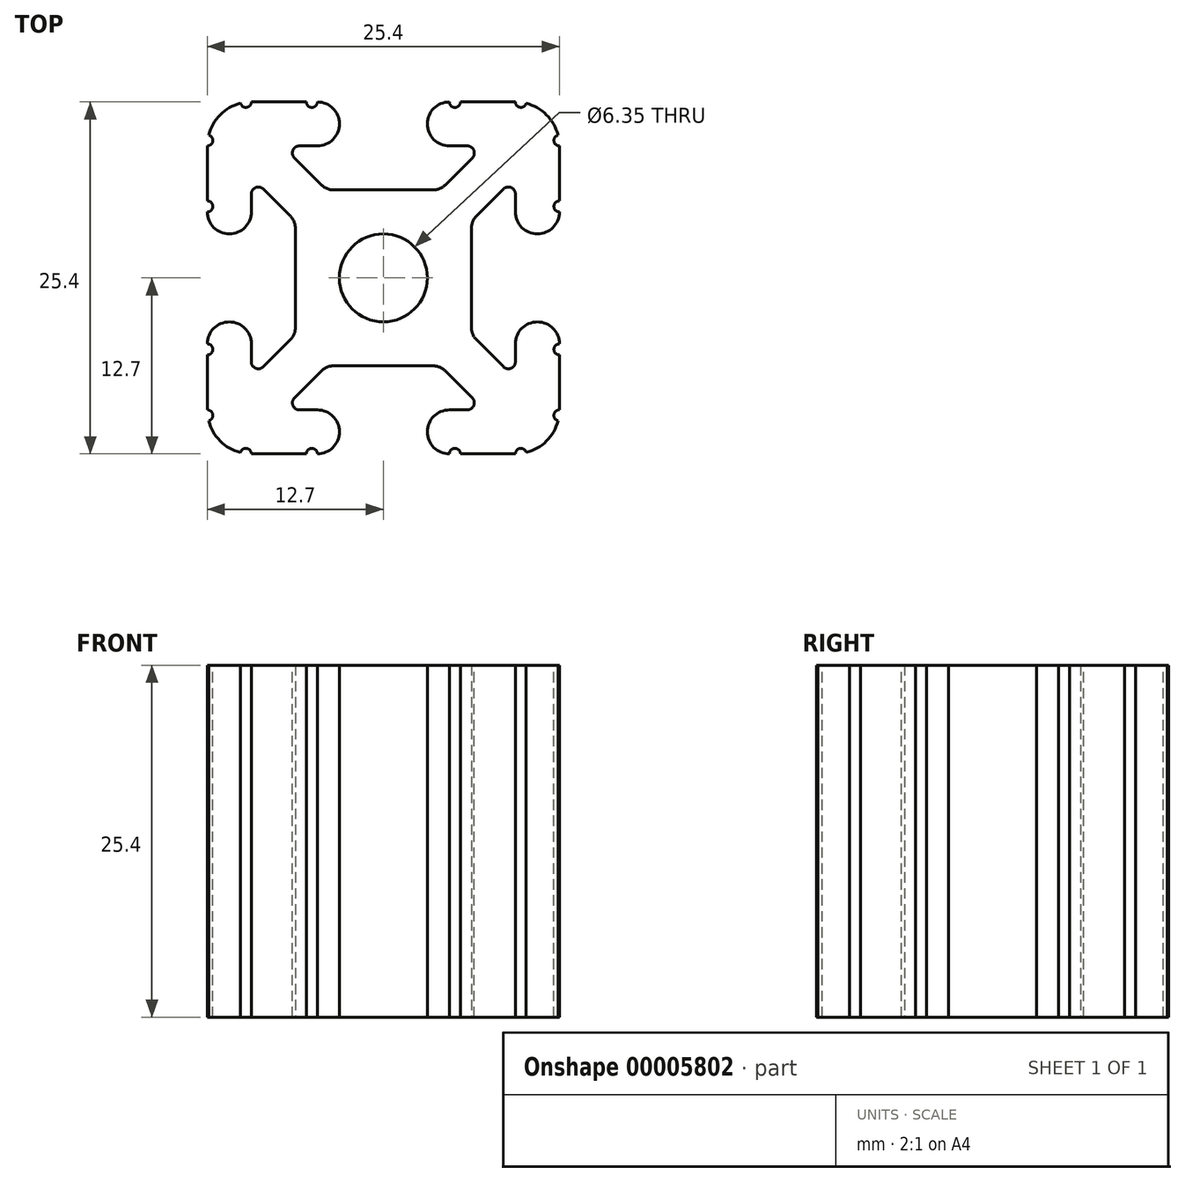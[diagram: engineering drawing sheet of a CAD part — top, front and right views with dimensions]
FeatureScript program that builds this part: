
annotation { "Feature Type Name" : "Feature", "Feature Type Description" : "" }
export const myFeature = defineFeature(function(context is Context, id is Id, definition is map)
    precondition{}
    {
        {
            var Q0;
            Q0=qCreatedBy(makeId("Top.planeOp"),FACE);
            var sketch = newSketch(context, id + "F0", { "sketchPlane" : qUnion([Q0])});
            skArc(sketch, "E0", {"start": v(0, 3.18) * mm, "mid": v(-2.25, 2.25) * mm, "end": v(-3.18, 0) * mm});
            skLineSegment(sketch, "E1", {"start": v(-6.35, 0) * mm, "end": v(-6.35, 4.1) * mm});
            skLineSegment(sketch, "E2", {"start": v(-6.35, 4.1) * mm, "end": v(-9.53, 7.28) * mm});
            skLineSegment(sketch, "E3", {"start": v(-9.53, 7.28) * mm, "end": v(-9.53, 4.76) * mm});
            skArc(sketch, "E4", {"start": v(-12.7, 4.76) * mm, "mid": v(-11.11, 3.17) * mm, "end": v(-9.52, 4.76) * mm});
            skLineSegment(sketch, "E5", {"start": v(-12.7, 4.76) * mm, "end": v(-12.7, 9.52) * mm});
            skArc(sketch, "E6", {"start": v(-9.53, 12.7) * mm, "mid": v(-11.77, 11.77) * mm, "end": v(-12.7, 9.52) * mm});
            skLineSegment(sketch, "E7", {"start": v(-9.53, 12.7) * mm, "end": v(-4.76, 12.7) * mm});
            skArc(sketch, "E8", {"start": v(-4.76, 9.53) * mm, "mid": v(-3.18, 11.11) * mm, "end": v(-4.76, 12.7) * mm});
            skLineSegment(sketch, "E9", {"start": v(-4.76, 9.53) * mm, "end": v(-7.28, 9.53) * mm});
            skLineSegment(sketch, "E10", {"start": v(-7.28, 9.53) * mm, "end": v(-4.1, 6.35) * mm});
            skLineSegment(sketch, "E11", {"start": v(-4.1, 6.35) * mm, "end": v(0, 6.35) * mm});
            skLineSegment(sketch, "E12", {"start": v(0, 6.35) * mm, "end": v(0, 3.18) * mm});
            skLineSegment(sketch, "E13", {"start": v(-3.18, 0) * mm, "end": v(-6.35, 0) * mm});
            skLineSegment(sketch, "E14", {"start": v(-3.18, 0) * mm, "end": v(-3.18, 11.11) * mm, "construction": true});
            skSolve(sketch);
        }
        {
            var Q0;
            Q0=makeQuery(id+"F0.imprint","IMPRINT",FACE,{"disambiguationData":[TD([[makeQuery(id+"F0.imprint","IMPRINT",EDGE,{"derivedFrom":sQuery(id+"F0.wireOp",EDGE,"E0")}),-1.0]])]});
            extrude(context, id + "F1", {"entities" : qUnion([Q0]), "depth" : 25.4 * mm});
        }
        {
            var Q0;
            Q0=makeQuery(id+"F1.opExtrude","SWEPT_EDGE",EDGE,{"disambiguationData":[OSD([sQuery(id+"F0.wireOp",EDGE,"E2"),sQuery(id+"F0.wireOp",EDGE,"E3")])]});
            var Q1;
            Q1=makeQuery(id+"F1.opExtrude","SWEPT_EDGE",EDGE,{"disambiguationData":[OSD([sQuery(id+"F0.wireOp",EDGE,"E9"),sQuery(id+"F0.wireOp",EDGE,"E10")])]});
            fillet(context, id + "F2", {"entities" : qUnion([Q0, Q1]), "radius" : 0.5 * mm, "tangentPropagation" : true, "allowEdgeOverflow" : false});
        }
        {
            var Q0;
            Q0=makeQuery(id+"F1.opExtrude","SWEPT_EDGE",EDGE,{"disambiguationData":[OSD([sQuery(id+"F0.wireOp",EDGE,"E1"),sQuery(id+"F0.wireOp",EDGE,"E2")])]});
            var Q1;
            Q1=makeQuery(id+"F1.opExtrude","SWEPT_EDGE",EDGE,{"disambiguationData":[OSD([sQuery(id+"F0.wireOp",EDGE,"E10"),sQuery(id+"F0.wireOp",EDGE,"E11")])]});
            fillet(context, id + "F3", {"entities" : qUnion([Q0, Q1]), "radius" : 1.27 * mm, "tangentPropagation" : true, "allowEdgeOverflow" : false});
        }
        {
            var Q0;
            Q0=qCreatedBy(makeId("Front.planeOp"),FACE);
            var sketch = newSketch(context, id + "F4", { "sketchPlane" : qUnion([Q0])});
            skLineSegment(sketch, "E15", {"start": v(0, 0) * mm, "end": v(0, 25.4) * mm, "construction": true});
            skSolve(sketch);
        }
        {
            var Q0;
            Q0=makeQuery(id+"F1.opExtrude","CAP_FACE",FACE,{"disambiguationData":[OSD([sQuery(id+"F0.wireOp",EDGE,"E0"),sQuery(id+"F0.wireOp",EDGE,"E1"),sQuery(id+"F0.wireOp",EDGE,"E2"),sQuery(id+"F0.wireOp",EDGE,"E3"),sQuery(id+"F0.wireOp",EDGE,"E4"),sQuery(id+"F0.wireOp",EDGE,"E5"),sQuery(id+"F0.wireOp",EDGE,"E6"),sQuery(id+"F0.wireOp",EDGE,"E7"),sQuery(id+"F0.wireOp",EDGE,"E8"),sQuery(id+"F0.wireOp",EDGE,"E9"),sQuery(id+"F0.wireOp",EDGE,"E10"),sQuery(id+"F0.wireOp",EDGE,"E11"),sQuery(id+"F0.wireOp",EDGE,"E12"),sQuery(id+"F0.wireOp",EDGE,"E13")])],"isStart":false});
            var sketch = newSketch(context, id + "F5", { "sketchPlane" : qUnion([Q0])});
            skLineSegment(sketch, "E16.0", {"start": v(-5.56, 12.7) * mm, "end": v(-4.76, 12.7) * mm});
            skArc(sketch, "E17", {"start": v(-5.56, 12.7) * mm, "mid": v(-5.16, 12.3) * mm, "end": v(-4.76, 12.7) * mm});
            skArc(sketch, "E18.0", {"start": v(-9.53, 12.7) * mm, "mid": v(-9.92, 12.68) * mm, "end": v(-10.3, 12.6) * mm});
            skArc(sketch, "E19", {"start": v(-10.3, 12.6) * mm, "mid": v(-9.87, 12.3) * mm, "end": v(-9.53, 12.7) * mm});
            skPoint(sketch, "E20.orphan", {"position": v(-12.7, 9.52) * mm});
            skLineSegment(sketch, "E21", {"start": v(-9.53, 9.52) * mm, "end": v(0, 0) * mm, "construction": true});
            skArc(sketch, "E22.0.MirrorCS", {"start": v(-12.6, 10.3) * mm, "mid": v(-12.3, 9.87) * mm, "end": v(-12.7, 9.52) * mm});
            skArc(sketch, "E22.1.MirrorCS", {"start": v(-12.7, 9.52) * mm, "mid": v(-12.68, 9.92) * mm, "end": v(-12.6, 10.3) * mm});
            skLineSegment(sketch, "E23.0.MirrorCS", {"start": v(-12.7, 5.56) * mm, "end": v(-12.7, 4.76) * mm});
            skArc(sketch, "E23.1.MirrorCS", {"start": v(-12.7, 5.56) * mm, "mid": v(-12.3, 5.16) * mm, "end": v(-12.7, 4.76) * mm});
            skSolve(sketch);
        }
        {
            var Q0;
            Q0 = qSketchRegion(id + "F5", true);
            extrude(context, id + "F6", {"entities" : qUnion([Q0]), "operationType" : NewBodyOperationType.REMOVE, "oppositeDirection" : true, "depth" : 25.4 * mm});
        }
        {
            var Q0;
            Q0=makeQuery(id+"F1.opExtrude","SWEPT_BODY",BODY,{"disambiguationData":[OSD([sQuery(id+"F0.wireOp",EDGE,"E0"),sQuery(id+"F0.wireOp",EDGE,"E1"),sQuery(id+"F0.wireOp",EDGE,"E2"),sQuery(id+"F0.wireOp",EDGE,"E3"),sQuery(id+"F0.wireOp",EDGE,"E4"),sQuery(id+"F0.wireOp",EDGE,"E5"),sQuery(id+"F0.wireOp",EDGE,"E6"),sQuery(id+"F0.wireOp",EDGE,"E7"),sQuery(id+"F0.wireOp",EDGE,"E8"),sQuery(id+"F0.wireOp",EDGE,"E9"),sQuery(id+"F0.wireOp",EDGE,"E10"),sQuery(id+"F0.wireOp",EDGE,"E11"),sQuery(id+"F0.wireOp",EDGE,"E12"),sQuery(id+"F0.wireOp",EDGE,"E13")])]});
            var Q1;
            Q1=sQuery(id+"F4.wireOp",EDGE,"E15");
            circularPattern(context, id + "F7", {"operationType" : NewBodyOperationType.ADD, "entities" : qUnion([Q0]), "axis" : qUnion([Q1]), "angle" : 90 * degree, "instanceCount" : 4});
        }
    });
